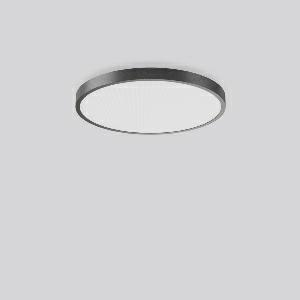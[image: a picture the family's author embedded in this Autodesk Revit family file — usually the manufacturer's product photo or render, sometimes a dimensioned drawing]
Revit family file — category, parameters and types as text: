
# Revit family: triona_round_a_312296_0031_730_c250
name_source: partatom
category: Lighting Fixtures
units: mm (PartAtom-declared; Revit-internal decimal feet)

## family parameters
Cut with Voids When Loaded = No
Host = Face
Light Source = No
Part Type = Normal
Room Calculation Point = No
Round Connector Dimension = Use Diameter
Shared = No

## types (1)
- TRIONA round A (1 x LED Modul 830, 3750 lm, 3000)
    Apparent Load = 31 VA
    CIE Flux Codes = 58 86 97 100 100
    Color Rendering = 80
    Color Temperature = 3000
    Default Elevation = 1800 mm
    Description = Series: TRIONA round
Decorative round LED surface-mounted luminaire. Flat, seamless frame: aluminium extrusion profile, powder coated. Cover made of sheet steel, powder-coated. Light emission through a diffuser in plastic, opal/prismatic. Lightguide and diffuser made of non-yellowing plastic (PMMA). Lateral light emission (RZB SIDELITE technology) for above-average homogeneous light distribution. Suitable for Ceiling mounting, Wall (surface). Tool-free mounting via bayonet connection. Electronic ballast included. Very easy installation thanks to Plug+Play connection. With Casambi smart+free Bluetooth control for wireless network and operation using Android / iOS devices, free app available for download. Perfect for office areas (RUG < 19) and environments with computer screens in accordance with EN 12464-1. 
Colour: anthracite metallic (DB703)
Diameter: 681 mm
Height: 88 mm
Lamp: LED
Socket: without socket
Colour temperature: 3000K
Colour rendering index (CRI): 80
System power: 31 W
Rated luminous flux: 3750 lm
Luminous efficiency: 121 lm/W
Control gear: Dimmable Bluetooth converter
Protection class: I
Type of protection: IP 20
    Height = 88 mm
    Lamp = 1 x LED Modul 830
    Lamp Light Flux = 3750 lm
    Lamp count = 1
    Length = 681 mm
    Lifetime = 50000 h
    Luminous efficacy = 121 lm/W
    Manufacturer = RZB
    ModVariant = No
    Model = 312296.0031.730
    Mounting Place = Ceiling
    Mounting Type = Surface mounted
    Number of Poles = 1
    OnlyDefault = Yes
    Power Factor = 1
    Product Name = TRIONA round A
    Product group = Surface mounted modular luminaires
    ProductGroupID = 306
    Protection Class = Protection class I
    Protection Degree = IP 20
    RLX_Detail_Level = 1
    RLX_Emergency_Light_Flux = 0 lm
    RLX_Emergency_Type = 0
    RLX_Emergency_Type_DB = No
    RlxData = <blob elided: 35225 chars, md5=9c7cad26>
    Socket = socket
    Standby Power = 0 W
    System Light Flux = 3750 lm
    System Power = 31 W
    Type Comments = Product without accessories
    Type Image = 312297.0031.jpg
    URL = http://relux.com
    VarID = ---
    Voltage = 230 V
    Voltage Range = 220-240 V
    Weight = 0.00 kg
    Width = 0 mm  [stored 0 ft]

note: [stored X ft] marks values corroborated as IEEE doubles in the binary element streams (Revit-internal decimal feet)

## geometry (parser evidence)
native form markers: Blend x4, Sweep x8
no freeform markers — native parametric forms only
